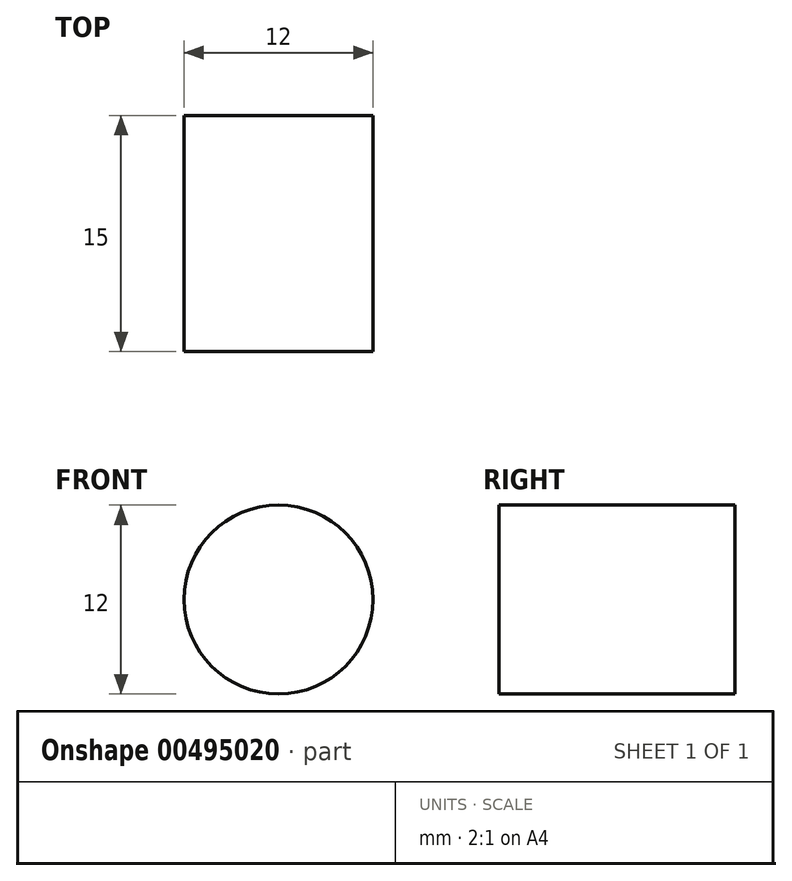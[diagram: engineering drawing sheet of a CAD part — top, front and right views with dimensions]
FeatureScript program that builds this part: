
annotation { "Feature Type Name" : "Feature", "Feature Type Description" : "" }
export const myFeature = defineFeature(function(context is Context, id is Id, definition is map)
    precondition{}
    {
        {
            var Q0;
            Q0=qCreatedBy(makeId("Front.planeOp"),FACE);
            var sketch = newSketch(context, id + "F0", { "sketchPlane" : qUnion([Q0])});
            skCircle(sketch, "E0", {"center": v(0, 0) * mm, "radius": 6 * mm});
            skSolve(sketch);
        }
        {
            var Q0;
            Q0=makeQuery(id+"F0.imprint","IMPRINT",FACE,{"disambiguationData":[TD([[makeQuery(id+"F0.imprint","IMPRINT",EDGE,{"derivedFrom":sQuery(id+"F0.wireOp",EDGE,"E0")}),1.0]])]});
            extrude(context, id + "F1", {"entities" : qUnion([Q0]), "depth" : 15 * mm, "offsetDistance" : 25.4 * mm});
        }
    });
